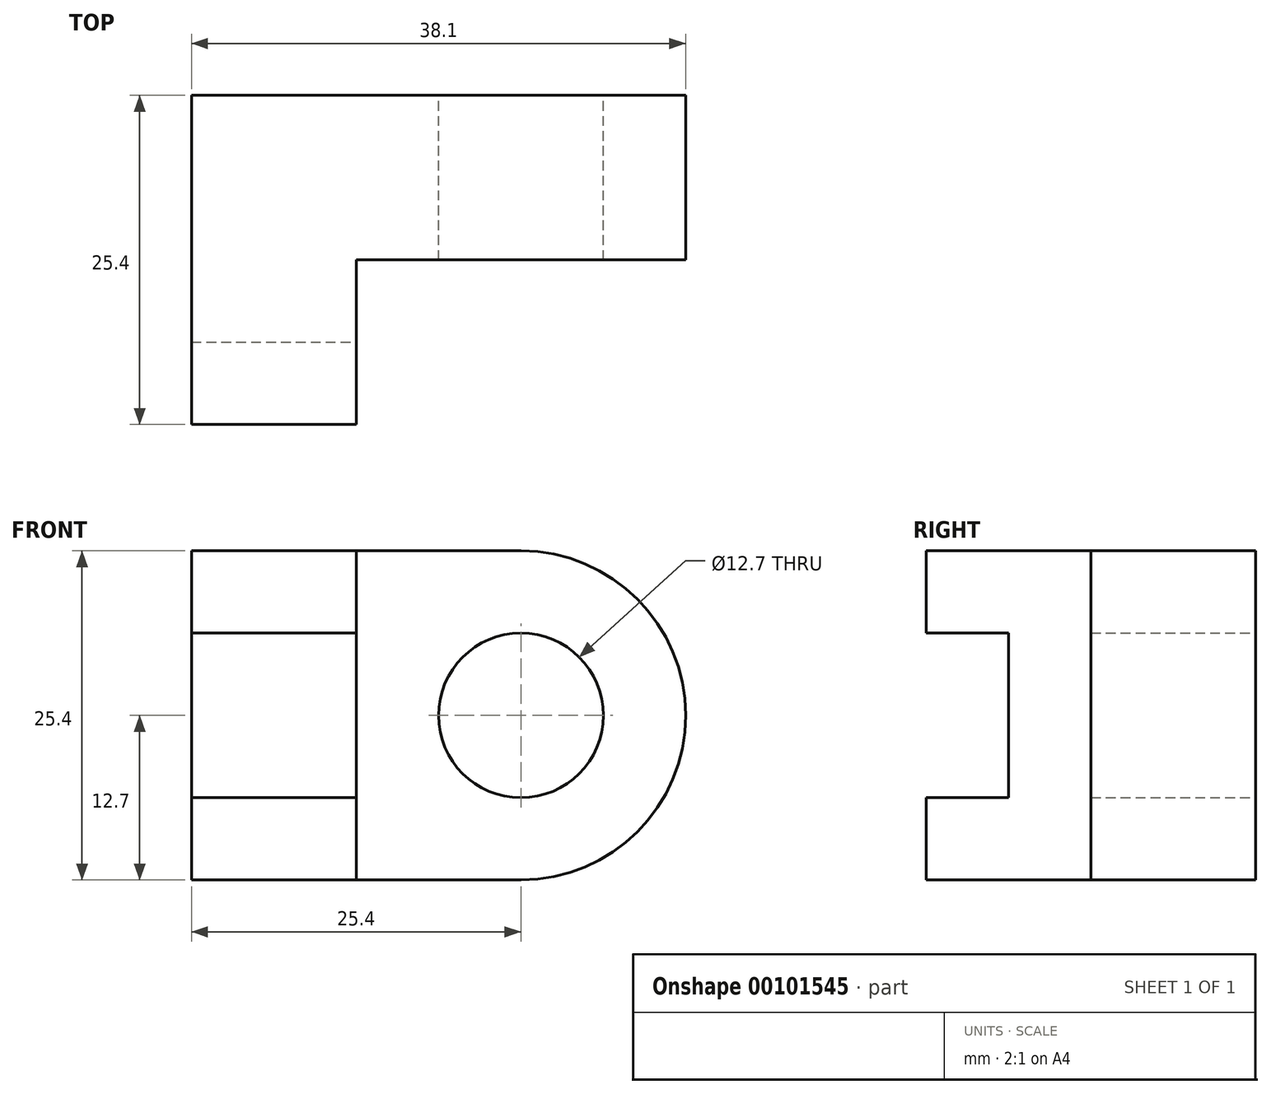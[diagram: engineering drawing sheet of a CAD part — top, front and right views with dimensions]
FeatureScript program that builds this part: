
annotation { "Feature Type Name" : "Feature", "Feature Type Description" : "" }
export const myFeature = defineFeature(function(context is Context, id is Id, definition is map)
    precondition{}
    {
        {
            var Q0;
            Q0=qCreatedBy(makeId("Right.planeOp"),FACE);
            var sketch = newSketch(context, id + "F0", { "sketchPlane" : qUnion([Q0])});
            skLineSegment(sketch, "E0", {"start": v(-25.4, 0) * mm, "end": v(-25.4, 6.35) * mm});
            skLineSegment(sketch, "E1", {"start": v(-25.4, 6.35) * mm, "end": v(-19.05, 6.35) * mm});
            skLineSegment(sketch, "E2", {"start": v(-19.05, 6.35) * mm, "end": v(-19.05, 19.05) * mm});
            skLineSegment(sketch, "E3", {"start": v(-19.05, 19.05) * mm, "end": v(-25.4, 19.05) * mm});
            skLineSegment(sketch, "E4", {"start": v(-25.4, 19.05) * mm, "end": v(-25.4, 25.4) * mm});
            skLineSegment(sketch, "E5", {"start": v(-25.4, 25.4) * mm, "end": v(0, 25.4) * mm});
            skLineSegment(sketch, "E6", {"start": v(0, 25.4) * mm, "end": v(0, 0) * mm});
            skLineSegment(sketch, "E7", {"start": v(0, 0) * mm, "end": v(-25.4, 0) * mm});
            skSolve(sketch);
        }
        {
            var Q0;
            Q0=makeQuery(id+"F0.imprint","IMPRINT",FACE,{"disambiguationData":[TD([[makeQuery(id+"F0.imprint","IMPRINT",EDGE,{"derivedFrom":sQuery(id+"F0.wireOp",EDGE,"E0")}),-1.0]])]});
            extrude(context, id + "F1", {"entities" : qUnion([Q0]), "oppositeDirection" : true, "depth" : 12.7 * mm});
        }
        {
            var Q0;
            Q0=qCreatedBy(makeId("Front.planeOp"),FACE);
            var sketch = newSketch(context, id + "F2", { "sketchPlane" : qUnion([Q0])});
            skLineSegment(sketch, "E8", {"start": v(0, 0) * mm, "end": v(0, 25.4) * mm});
            skLineSegment(sketch, "E9", {"start": v(0, 25.4) * mm, "end": v(12.7, 25.4) * mm});
            skLineSegment(sketch, "E10", {"start": v(12.7, 0) * mm, "end": v(0, 0) * mm});
            skArc(sketch, "E11", {"start": v(12.7, 0) * mm, "mid": v(25.4, 12.7) * mm, "end": v(12.7, 25.4) * mm});
            skCircle(sketch, "E12", {"center": v(12.7, 12.7) * mm, "radius": 6.35 * mm});
            skSolve(sketch);
        }
        {
            var Q0;
            Q0=makeQuery(id+"F2.imprint","IMPRINT",FACE,{"disambiguationData":[TD([[makeQuery(id+"F2.imprint","IMPRINT",EDGE,{"derivedFrom":sQuery(id+"F2.wireOp",EDGE,"E8")}),-1.0]])]});
            extrude(context, id + "F3", {"entities" : qUnion([Q0]), "operationType" : NewBodyOperationType.ADD, "depth" : 12.7 * mm});
        }
    });
